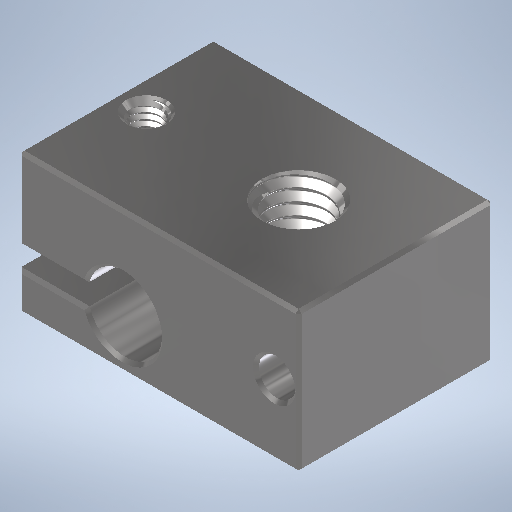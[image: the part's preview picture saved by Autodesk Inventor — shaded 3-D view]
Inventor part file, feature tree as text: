
AUTODESK INVENTOR PART (.ipt)
format: ipt  version: 2025.2 (Build 292293000, 293)  size: 2,365,952 bytes
history: native  units: mm
features: sketch x6, extrude x5, revolve x3, helix x3, chamfer x3
ambient origin geometry x8: Origin, YZ Plane, XZ Plane, XY Plane, X Axis, Y Axis, Z Axis, Center Point
bodies: Solid1 (feature_tree), Solid2 (feature_tree), Solid3 (feature_tree), Solid4 (feature_tree)
feature tree (20):
  extrude  "Extrusion1"  Depth=16.0mm
  extrude  "Extrusion2"  Depth=3.0mm
  extrude  "Extrusion3"  Depth=11.5mm TaperAngle=0.0deg
  extrude  "Extrusion4"  Depth=6.1mm
  revolve  "Revolution1"  [1 undecoded]
  helix  "Coil1"  [1 undecoded]
  revolve  "Revolution2"  [1 undecoded]
  chamfer  "Chamfer2"  Angle=60.0deg  [1 undecoded]
  helix  "Coil2"  [1 undecoded]
  revolve  "Revolution3"  [1 undecoded]
  extrude  "Extrusion5"  Depth=10.0mm TaperAngle=60.0deg
  helix  "Coil3"  [1 undecoded]
  chamfer  "Chamfer1"  Angle=60.0deg  [1 undecoded]
  chamfer  "Chamfer3"  [1 undecoded]
  sketch  "Sketch2"  dims[d0=23.0mm d1=16.0mm]
  sketch  "Sketch3"  dims[d2=11.5mm d3=0.0mm d5=3.0mm]
  sketch  "Sketch4"  dims[d6=6.0mm d7=11.5mm d8=0.0mm]
  sketch  "Sketch6"  dims[d9=3.0mm d10=6.1mm]
  sketch  "Sketch8"  dims[d11=11.5mm d12=0.0mm d13=3.0mm d14=11.5mm d15=0.0mm]
  sketch  "Sketch10"  dims[d22=60.0deg d23=0.160083mm d24=0.160083mm d27=1.0mm d29=60.0deg d31=0.0mm d32=1.001mm d33=13.5mm d34=10.0mm d35=0.0mm d36=0.0mm d37=0.0mm d38=0.0mm d39=0.0mm d40=0.7mm d42=60.0deg d43=0.080042mm d44=0.080042mm d47=0.5mm d49=60.0deg d51=0.0mm d52=0.5005mm d53=7.703146mm d54=10.0mm d55=0.0mm d56=0.0mm d57=0.0mm d58=0.0mm d59=0.0mm d60=0.5mm d62=45.0deg d63=60.0deg d64=0.080042mm d65=0.080042mm d68=0.5mm d70=60.0deg d72=0.0mm d73=0.5005mm d74=6.75mm d75=10.0mm d76=0.0mm d77=0.0mm d78=0.0mm d79=0.0mm d80=0.0mm d81=0.5mm d82=135.0deg d83=0.174mm d84=2.0mm d85=45.0deg d86=0.047mm d87=2.0mm d88=45.0deg d89=0.25mm d90=2.0mm d91=45.0deg d92=5.75mm d96=5.75mm d97=0.0mm]
note: 9 required parameter values undecoded (feature->parameter linkage not recoverable at this tier; creation-order binding heuristic only, values carry confidence <= 0.55)